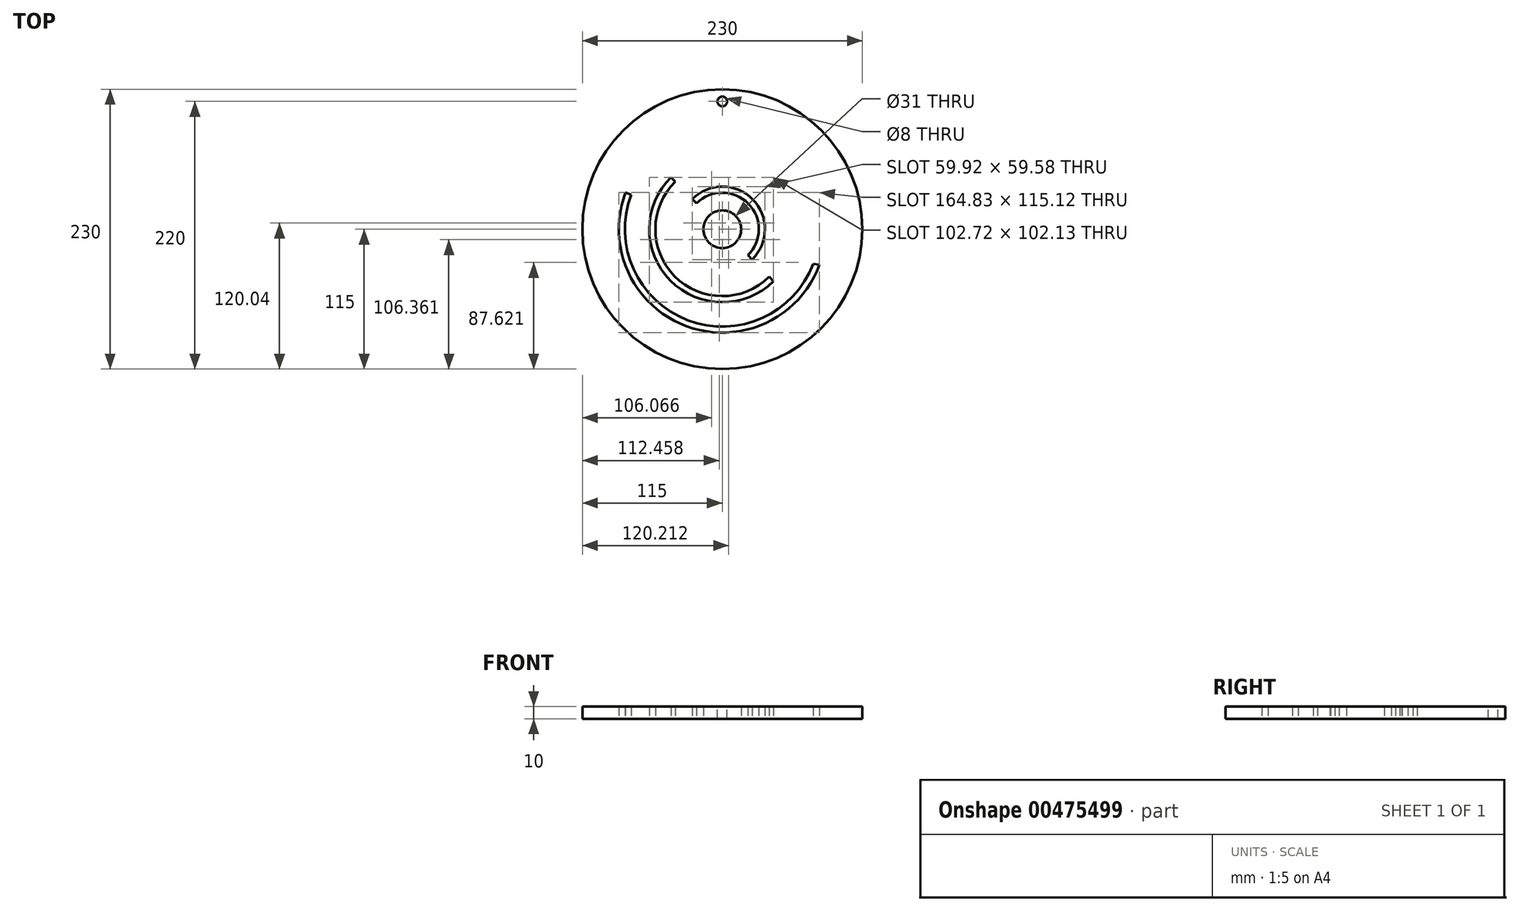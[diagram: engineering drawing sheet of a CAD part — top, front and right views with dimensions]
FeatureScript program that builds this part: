
annotation { "Feature Type Name" : "Feature", "Feature Type Description" : "" }
export const myFeature = defineFeature(function(context is Context, id is Id, definition is map)
    precondition{}
    {
        {
            var Q0;
            Q0=qCreatedBy(makeId("Top.planeOp"),FACE);
            var sketch = newSketch(context, id + "F0", { "sketchPlane" : qUnion([Q0])});
            skArc(sketch, "E0", {"start": v(0, 115) * mm, "mid": v(-81.32, -81.32) * mm, "end": v(115, 0) * mm});
            skArc(sketch, "E1", {"start": v(-79.46, 30.18) * mm, "mid": v(-29.63, -79.67) * mm, "end": v(79.87, -29.07) * mm});
            skArc(sketch, "E2", {"start": v(-74.78, 28.44) * mm, "mid": v(-28.44, -74.78) * mm, "end": v(74.78, -28.44) * mm});
            skCircle(sketch, "E3", {"center": v(0, 0) * mm, "radius": 115 * mm});
            skLineSegment(sketch, "E4", {"start": v(79.87, -29.07) * mm, "end": v(74.78, -28.44) * mm});
            skArc(sketch, "E5", {"start": v(24.58, -24.92) * mm, "mid": v(24.92, 24.58) * mm, "end": v(-24.58, 24.92) * mm});
            skArc(sketch, "E6", {"start": v(21.07, -21.36) * mm, "mid": v(21.36, 21.07) * mm, "end": v(-21.07, 21.36) * mm});
            skPoint(sketch, "E7.start.orphan", {"position": v(30, 0) * mm});
            skPoint(sketch, "E8.start.orphan", {"position": v(0, 30) * mm});
            skLineSegment(sketch, "E9", {"start": v(0, 0) * mm, "end": v(-114.26, 115.86) * mm, "construction": true});
            skLineSegment(sketch, "E10", {"start": v(0, 0) * mm, "end": v(114.37, -115.97) * mm, "construction": true});
            skLineSegment(sketch, "E11", {"start": v(21.07, -21.36) * mm, "end": v(24.58, -24.92) * mm});
            skLineSegment(sketch, "E12", {"start": v(-24.58, 24.92) * mm, "end": v(-21.07, 21.36) * mm});
            skCircle(sketch, "E13", {"center": v(0, 0) * mm, "radius": 15.5 * mm});
            skLineSegment(sketch, "E14", {"start": v(79.87, -29.07) * mm, "end": v(-89.23, 33.8) * mm, "construction": true});
            skLineSegment(sketch, "E15", {"start": v(-74.78, 28.44) * mm, "end": v(-79.46, 30.18) * mm});
            skPoint(sketch, "E16.orphan", {"position": v(-72.5, 33.8) * mm});
            skPoint(sketch, "E17.start.orphan", {"position": v(-23.14, 55.36) * mm});
            skArc(sketch, "E18", {"start": v(-38.62, 39.16) * mm, "mid": v(-39.16, -38.62) * mm, "end": v(38.62, -39.16) * mm});
            skArc(sketch, "E19", {"start": v(-42.13, 42.72) * mm, "mid": v(-42.72, -42.13) * mm, "end": v(42.13, -42.72) * mm});
            skPoint(sketch, "E20.orphan", {"position": v(-23.14, 73.24) * mm});
            skLineSegment(sketch, "E21.trimOffspring", {"start": v(-0.2, 0.2) * mm, "end": v(-0.38, 0.77) * mm, "construction": true});
            skLineSegment(sketch, "E22", {"start": v(-38.62, 39.16) * mm, "end": v(-42.13, 42.72) * mm});
            skLineSegment(sketch, "E23", {"start": v(42.13, -42.72) * mm, "end": v(38.62, -39.16) * mm});
            skSolve(sketch);
        }
        {
            var Q0;
            Q0 = qSketchRegion(id + "F0", true);
            extrude(context, id + "F1", {"entities" : qUnion([Q0]), "depth" : 10 * mm, "offsetDistance" : 25 * mm});
        }
        {
            var Q0;
            Q0=makeQuery(id+"F1.opExtrude","CAP_FACE",FACE,{"disambiguationData":[OSD([sQuery(id+"F0.wireOp",EDGE,"E1"),sQuery(id+"F0.wireOp",EDGE,"E2"),sQuery(id+"F0.wireOp",EDGE,"VrNfs41g-2vrx-tY6u-Kpo4-RobxseQNsVHP"),sQuery(id+"F0.wireOp",EDGE,"7nELppnV-BOAs-FJlg-orbO-PaPKTsrYaRbk"),sQuery(id+"F0.wireOp",EDGE,"G7ZyeyLv-fdAy-63HL-pTYy-QTd4YvWoU18D"),sQuery(id+"F0.wireOp",EDGE,"B4yyGxwv-4N1C-yBeA-tiS9-kJ8ohQssV4ua"),sQuery(id+"F0.wireOp",EDGE,"E3"),sQuery(id+"F0.wireOp",EDGE,"E17"),sQuery(id+"F0.wireOp",EDGE,"CcudwO88-cSzR-9owK-jIbY-H1nxCQIdNHwF"),sQuery(id+"F0.wireOp",EDGE,"uInnNRgz-TdKd-xaa8-GVby-vfFJRhz4c9x2"),sQuery(id+"F0.wireOp",EDGE,"gKWORGvq-WHat-32X1-vv2p-VGNgj9UePbQ5"),sQuery(id+"F0.wireOp",EDGE,"74xN8fPM-Mlnu-27oj-UPsj-sLi4qO0ykMAn"),sQuery(id+"F0.wireOp",EDGE,"E4")])],"isStart":false});
            var sketch = newSketch(context, id + "F2", { "sketchPlane" : qUnion([Q0])});
            skLineSegment(sketch, "E24", {"start": v(0, 0) * mm, "end": v(0, 90.15) * mm, "construction": true});
            skCircle(sketch, "E25", {"center": v(0, 105) * mm, "radius": 4 * mm});
            skSolve(sketch);
        }
        {
            var Q0;
            Q0 = qSketchRegion(id + "F2", true);
            extrude(context, id + "F3", {"entities" : qUnion([Q0]), "operationType" : NewBodyOperationType.REMOVE, "oppositeDirection" : true, "depth" : 25 * mm, "offsetDistance" : 25 * mm});
        }
    });
